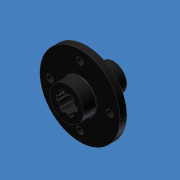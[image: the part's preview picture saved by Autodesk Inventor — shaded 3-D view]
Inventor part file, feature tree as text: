
AUTODESK INVENTOR PART (.ipt)
format: ipt  version: 2014 SP1 (Build 180222100, 222)  size: 203,776 bytes
history: native  units: mm (DEFAULTED — no unit token found)
features: sketch x8, extrude x5, hole x3, pattern_circular x2, fillet x1
ambient origin geometry x8: Origin, YZ Plane, XZ Plane, XY Plane, X Axis, Y Axis, Z Axis, Center Point
bodies: Solid1 (feature_tree)
feature tree (19):
  extrude  "Extrusion1"  Depth=6.35mm
  hole  "Mounting Hole"  [1 undecoded]
  pattern_circular  "Circular Pattern1"  Count=4 Angle=360.0deg
  extrude  "Extrusion2"  Depth=12.7mm TaperAngle=0.0deg
  hole  "Hole3"  [1 undecoded]
  extrude  "Extrusion3"  Depth=25.4mm
  pattern_circular  "Circular Pattern2"  [2 undecoded]
  extrude  "Extrusion4"  Depth=28.575mm TaperAngle=0.0deg
  extrude  "Extrusion5"  Depth=0.508mm
  hole  "Hole2"  [1 undecoded]
  fillet  "Fillet1"  Radius=4.0mm
  sketch  "Sketch1"  dims[d0=6.35mm d1=0.0mm d2=76.2mm]
  sketch  "Sketch2"  dims[d3=0.0mm d4=28.575mm]
  sketch  "Sketch3"  dims[d5=6.35mm d6=12.7mm d7=9.525mm d8=6.35mm d9=14.3117mm d10=19.05mm d11=20.594885mm d12=40.0mm d14=360.0deg]
  sketch  "Sketch4"  dims[d15=31.75mm d17=12.7mm d18=0.0mm]
  sketch  "Sketch5"  dims[d22=12.7mm d23=0.0mm d24=60.0mm d26=360.0deg]
  sketch  "Sketch6"  dims[d27=29.845mm d28=25.4mm d29=-0.872665mm]
  sketch  "Sketch7"  dims[d31=16.0mm]
  sketch  "Sketch8"  dims[d32=4.7625mm d33=10.31875mm d34=28.575mm d35=0.0mm d36=9.525mm d37=12.7mm d38=9.525mm d39=6.35mm d40=14.3117mm d41=19.05mm d42=20.594885mm d43=0.508mm d46=60.0deg d47=4.0mm d48=20.0mm d49=16.2mm d50=12.7mm d51=9.525mm d52=6.35mm d53=14.3117mm d54=14.986mm d55=0.0mm]
note: 5 required parameter values undecoded (feature->parameter linkage not recoverable at this tier; creation-order binding heuristic only, values carry confidence <= 0.55)
